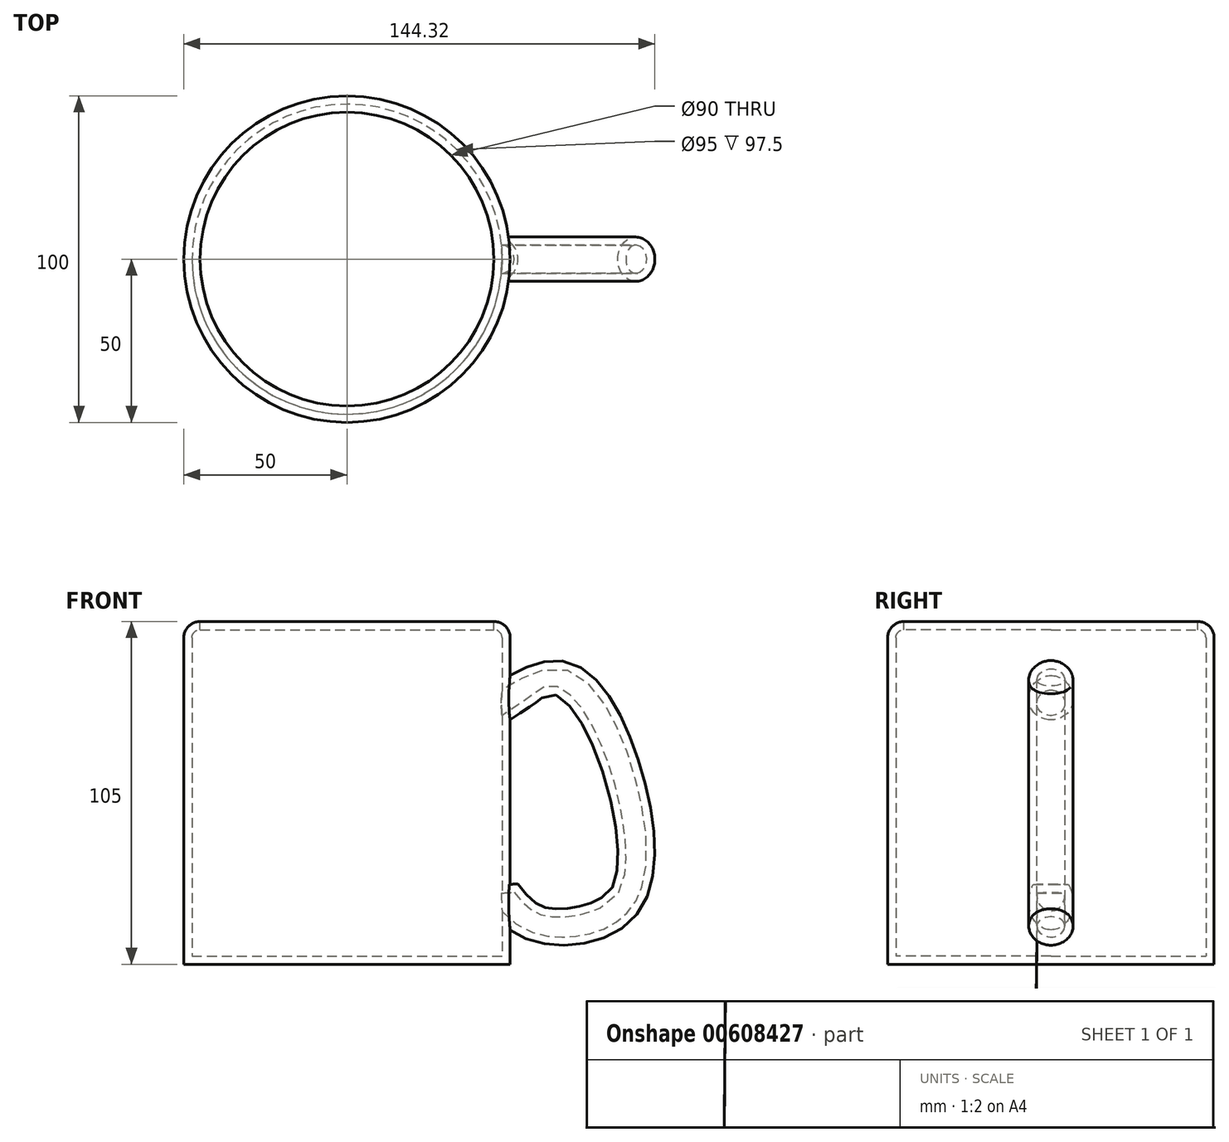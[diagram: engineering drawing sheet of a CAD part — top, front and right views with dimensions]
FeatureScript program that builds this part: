
annotation { "Feature Type Name" : "Feature", "Feature Type Description" : "" }
export const myFeature = defineFeature(function(context is Context, id is Id, definition is map)
    precondition{}
    {
        {
            var Q0;
            Q0=qCreatedBy(makeId("Top.planeOp"),FACE);
            var sketch = newSketch(context, id + "F0", { "sketchPlane" : qUnion([Q0])});
            skCircle(sketch, "E0", {"center": v(0, 0) * mm, "radius": 50 * mm});
            skSolve(sketch);
        }
        {
            var Q0;
            Q0 = qSketchRegion(id + "F0", true);
            extrude(context, id + "F1", {"entities" : qUnion([Q0]), "depth" : 105 * mm, "offsetDistance" : 25 * mm});
        }
        {
            var Q0;
            Q0=qCreatedBy(makeId("Front.planeOp"),FACE);
            var sketch = newSketch(context, id + "F2", { "sketchPlane" : qUnion([Q0])});
            skFitSpline(sketch, "E1", {"points": [v(45.14, 80.3) * mm, v(67.63, 87.79) * mm, v(87.63, 52.18) * mm, v(83.88, 16.56) * mm, v(57.64, 11.56) * mm, v(43.9, 24.06) * mm], "startDerivative": vector(128.73, 83.14) * mm, "endDerivative": vector(-67.1, 95.28) * mm});
            skSolve(sketch);
        }
        {
            var Q0;
            Q0=qCreatedBy(makeId("Right.planeOp"),FACE);
            cPlane(context, id + "F3", {"entities" : qUnion([Q0]), "cplaneType" : CPlaneType.OFFSET, "offset" : 50 * mm, "width" : 150 * mm, "height" : 150 * mm});
        }
        {
            var Q0;
            Q0=qCreatedBy(id+"F3.planeOp",FACE);
            var sketch = newSketch(context, id + "F4", { "sketchPlane" : qUnion([Q0])});
            skCircle(sketch, "E2", {"center": v(0, 81.65) * mm, "radius": 6.8 * mm});
            skSolve(sketch);
        }
        {
            var Q0;
            Q0=makeQuery(id+"F4.imprint","IMPRINT",FACE,{"disambiguationData":[TD([[makeQuery(id+"F4.imprint","IMPRINT",EDGE,{"derivedFrom":sQuery(id+"F4.wireOp",EDGE,"E2")}),1.0]])]});
            var Q1;
            Q1 = qConstructionFilter(qBodyType(qCreatedBy(id + "F2" ,EDGE), BodyType.WIRE), ConstructionObject.NO);
            sweep(context, id + "F5", {"operationType" : NewBodyOperationType.ADD, "profiles" : qUnion([Q0]), "path" : qUnion([Q1])});
        }
        {
            var Q0;
            Q0=makeQuery(id+"F1.opExtrude","CAP_FACE",FACE,{"disambiguationData":[OSD([sQuery(id+"F0.wireOp",EDGE,"E0")])],"isStart":false});
            fillet(context, id + "F6", {"entities" : qUnion([Q0]), "radius" : 5 * mm, "tangentPropagation" : true, "allowEdgeOverflow" : false});
        }
        {
            var Q0;
            Q0=makeQuery(id+"F1.opExtrude","CAP_FACE",FACE,{"disambiguationData":[OSD([sQuery(id+"F0.wireOp",EDGE,"E0")])],"isStart":false});
            shell(context, id + "F7", {"entities" : qUnion([Q0]), "thickness" : 2.5 * mm});
        }
    });
